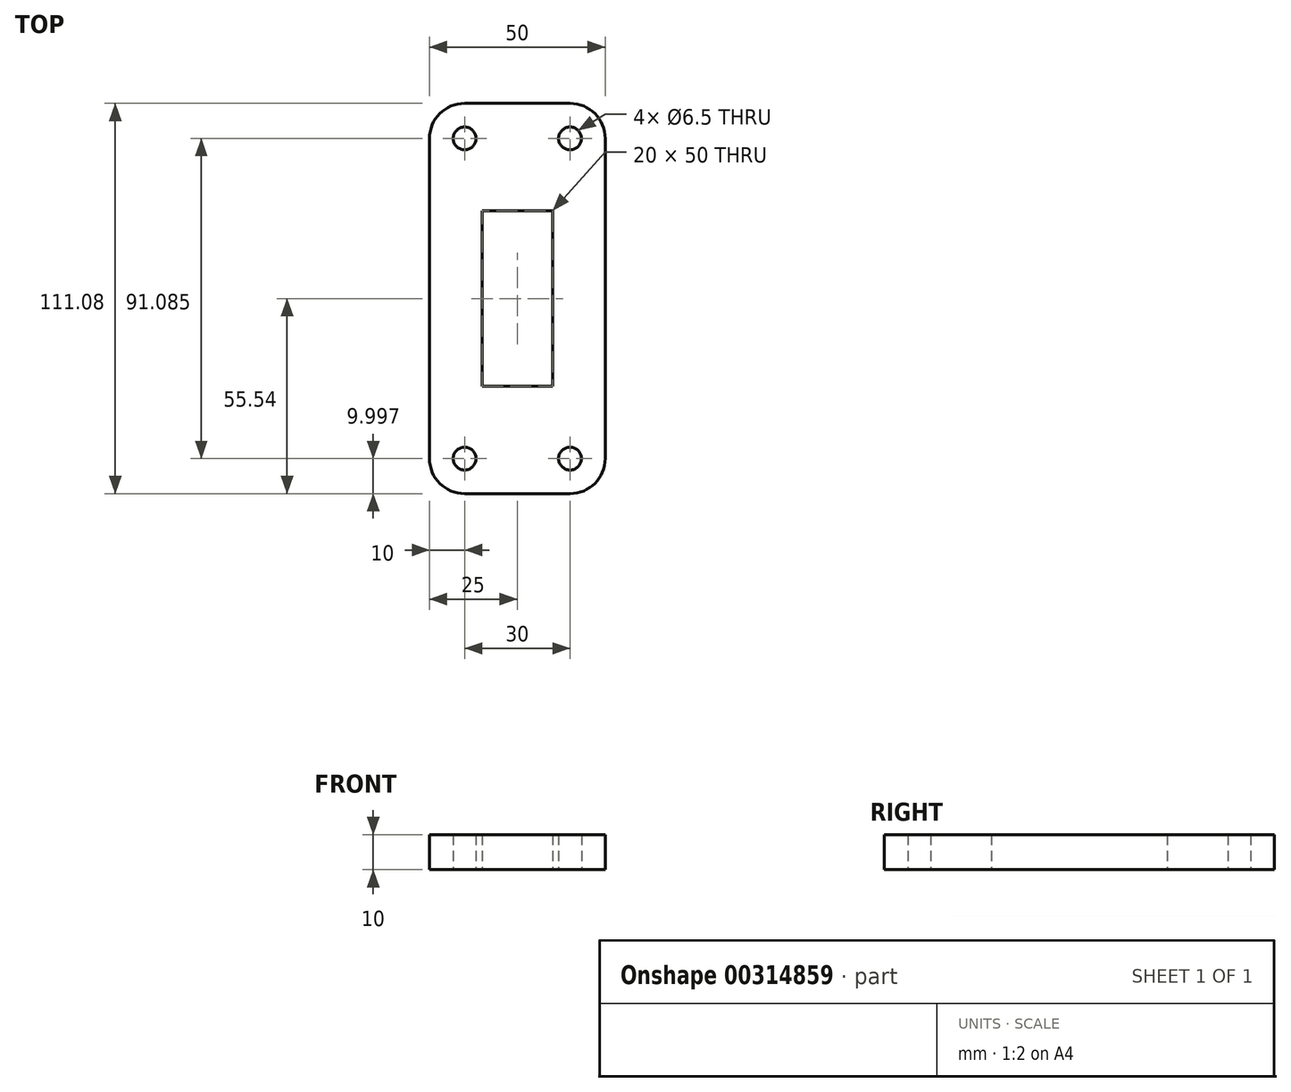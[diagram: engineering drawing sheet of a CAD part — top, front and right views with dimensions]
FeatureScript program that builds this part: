
annotation { "Feature Type Name" : "Feature", "Feature Type Description" : "" }
export const myFeature = defineFeature(function(context is Context, id is Id, definition is map)
    precondition{}
    {
        {
            var Q0;
            Q0=qCreatedBy(makeId("Top.planeOp"),FACE);
            var sketch = newSketch(context, id + "F0", { "sketchPlane" : qUnion([Q0])});
            skLineSegment(sketch, "E0.bottom", {"start": v(15, -55.54) * mm, "end": v(-15, -55.54) * mm});
            skLineSegment(sketch, "E0.top", {"start": v(15, 55.54) * mm, "end": v(-15, 55.54) * mm});
            skLineSegment(sketch, "E0.left", {"start": v(25, -45.54) * mm, "end": v(25, 45.54) * mm});
            skLineSegment(sketch, "E0.right", {"start": v(-25, -45.54) * mm, "end": v(-25, 45.54) * mm});
            skPoint(sketch, "E0.middle", {"position": v(0, 0) * mm});
            skPoint(sketch, "E1.visualSharp", {"position": v(-25, 55.54) * mm});
            skArc(sketch, "E1.filletArc", {"start": v(-15, 55.54) * mm, "mid": v(-22.07, 52.61) * mm, "end": v(-25, 45.54) * mm});
            skPoint(sketch, "E2.visualSharp", {"position": v(25, 55.54) * mm});
            skArc(sketch, "E2.filletArc", {"start": v(25, 45.54) * mm, "mid": v(22.07, 52.61) * mm, "end": v(15, 55.54) * mm});
            skPoint(sketch, "E3.visualSharp", {"position": v(-25, -55.54) * mm});
            skArc(sketch, "E3.filletArc", {"start": v(-25, -45.54) * mm, "mid": v(-22.07, -52.61) * mm, "end": v(-15, -55.54) * mm});
            skPoint(sketch, "E4.visualSharp", {"position": v(25, -55.54) * mm});
            skArc(sketch, "E4.filletArc", {"start": v(15, -55.54) * mm, "mid": v(22.07, -52.61) * mm, "end": v(25, -45.54) * mm});
            skLineSegment(sketch, "E5", {"start": v(-43.24, 0) * mm, "end": v(46.93, 0) * mm, "construction": true});
            skPoint(sketch, "E5.endSnap0", {"position": v(25, 0) * mm});
            skLineSegment(sketch, "E6.bottom", {"start": v(-10, -25) * mm, "end": v(10, -25) * mm});
            skLineSegment(sketch, "E6.top", {"start": v(-10, 25) * mm, "end": v(10, 25) * mm});
            skLineSegment(sketch, "E6.left", {"start": v(-10, -25) * mm, "end": v(-10, 25) * mm});
            skLineSegment(sketch, "E6.right", {"start": v(10, -25) * mm, "end": v(10, 25) * mm});
            skLineSegment(sketch, "E7", {"start": v(-12.94, 0) * mm, "end": v(7.06, 0) * mm, "construction": true});
            skCircle(sketch, "E8", {"center": v(-15, 45.54) * mm, "radius": 3.25 * mm});
            skCircle(sketch, "E9", {"center": v(15, 45.54) * mm, "radius": 3.25 * mm});
            skCircle(sketch, "E10", {"center": v(15, -45.54) * mm, "radius": 3.25 * mm});
            skCircle(sketch, "E11", {"center": v(-15, -45.54) * mm, "radius": 3.25 * mm});
            skSolve(sketch);
        }
        {
            var Q0;
            Q0=makeQuery(id+"F0.imprint","IMPRINT",FACE,{"disambiguationData":[TD([[makeQuery(id+"F0.imprint","IMPRINT",EDGE,{"derivedFrom":sQuery(id+"F0.wireOp",EDGE,"E0.bottom")}),-1.0]])]});
            extrude(context, id + "F1", {"entities" : qUnion([Q0]), "depth" : 10 * mm});
        }
    });
